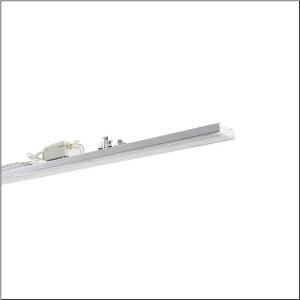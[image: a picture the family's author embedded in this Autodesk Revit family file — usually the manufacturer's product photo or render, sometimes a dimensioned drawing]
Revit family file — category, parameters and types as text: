
# Revit family: licross_21_recessed_mo_52tl19de445g
name_source: partatom
category: Lighting Fixtures
units: mm (PartAtom-declared; Revit-internal decimal feet)

## family parameters
Cut with Voids When Loaded = No
Host = Face
Light Source = No
Part Type = Normal
Room Calculation Point = No
Round Connector Dimension = Use Diameter
Shared = No

## types (1)
- --- (1 x LED, 4930 lm, 29.9 W, 4000K)
    Apparent Load = 30 VA
    CIE Flux Codes = 55 90 98 100 100
    Color Rendering = 80
    Color Temperature = 4000K
    Default Elevation = 1800 mm
    Description = Licross 21 Recessed MO, luminaire insert, of sheet steel, galvanised, coil coated, white, length: 750mm, width: 66mm, height: 67mm, LED rated luminous flux: 4.930lm, light colour: 840, SDCM (Standard Deviation of Colour Matching)MacAdam ≤ 3 SDCM (initial), control gear: DALI 2, with plug, 5-pole, with phase selection, mains connection: 220..240V, AC, 50/60Hz, rated input power: 30W, internal wiring halogen-free, primary light control with lens, of plastic, primary optical cover: cover, of PMMA, light emission: direct distribution, primary light characteristic: double asymmetric, protection rating (complete): IP40, insulation class (complete): insulation class I (protective earthing), certification: CE, ENEC, VDE, UKCA, protection symbol: D if used in an environment without relevant dust loads with corresponding accessories, impact resistance: IK06, permissible ambient temperature for indoor applications: -25..+35°C, corresponds to IFS (International Featured Standards) requirements for safety and quality in the food industry, reducing of maximum allowable ambient temperature of 5°C with ceiling mounting, LABS conformity tested according to VDMA 24364:2018-05, The light source and the operating device comply with the requirements of the Ecodesign Regulation (EU) 2019/2020 and are replaceable in accordance with this regulation, packaging unit: 1 piece
    Height = 58 mm
    Lamp = 1 x LED
    Lamp Light Flux = 4930 lm
    Lamp Power = 29.9 W
    Lamp count = 1
    Length = 750 mm
    Luminous efficacy = 165 lm/W
    Manufacturer = Siteco
    ModVariant = No
    Model = 52TL19DE445G
    Mounting Place = Ceiling
    Mounting Type = Pendant
    Number of Poles = 1
    OnlyDefault = Yes
    Power Factor = 1
    Product Name = Licross 21 Recessed MO
    Product group = luminaire insert | ceiling pendant
    ProductGroupID = 901
    Protection Class = Protection class I
    Protection Degree = IP 40
    RLX_Detail_Level = 1
    RLX_Emergency_Light_Flux = 0 lm
    RLX_Emergency_Type = 0
    RLX_Emergency_Type_DB = No
    RlxData = <blob elided: 29309 chars, md5=5f88205d>
    Socket = socket
    Standby Power = 0 W
    System Light Flux = 4930 lm
    System Power = 30 W
    Type Comments = factory setting: luminous flux: 100 % | dim-lin: 254 | 390 mA
    Type Image = l_1296930.jpg
    URL = http://relux.com
    VarID = @adj_129815
    Voltage = 0 V
    Weight = 0.00 kg
    Width = 66 mm

## geometry (parser evidence)
native form markers: Blend x4, Sweep x10
no freeform markers — native parametric forms only
